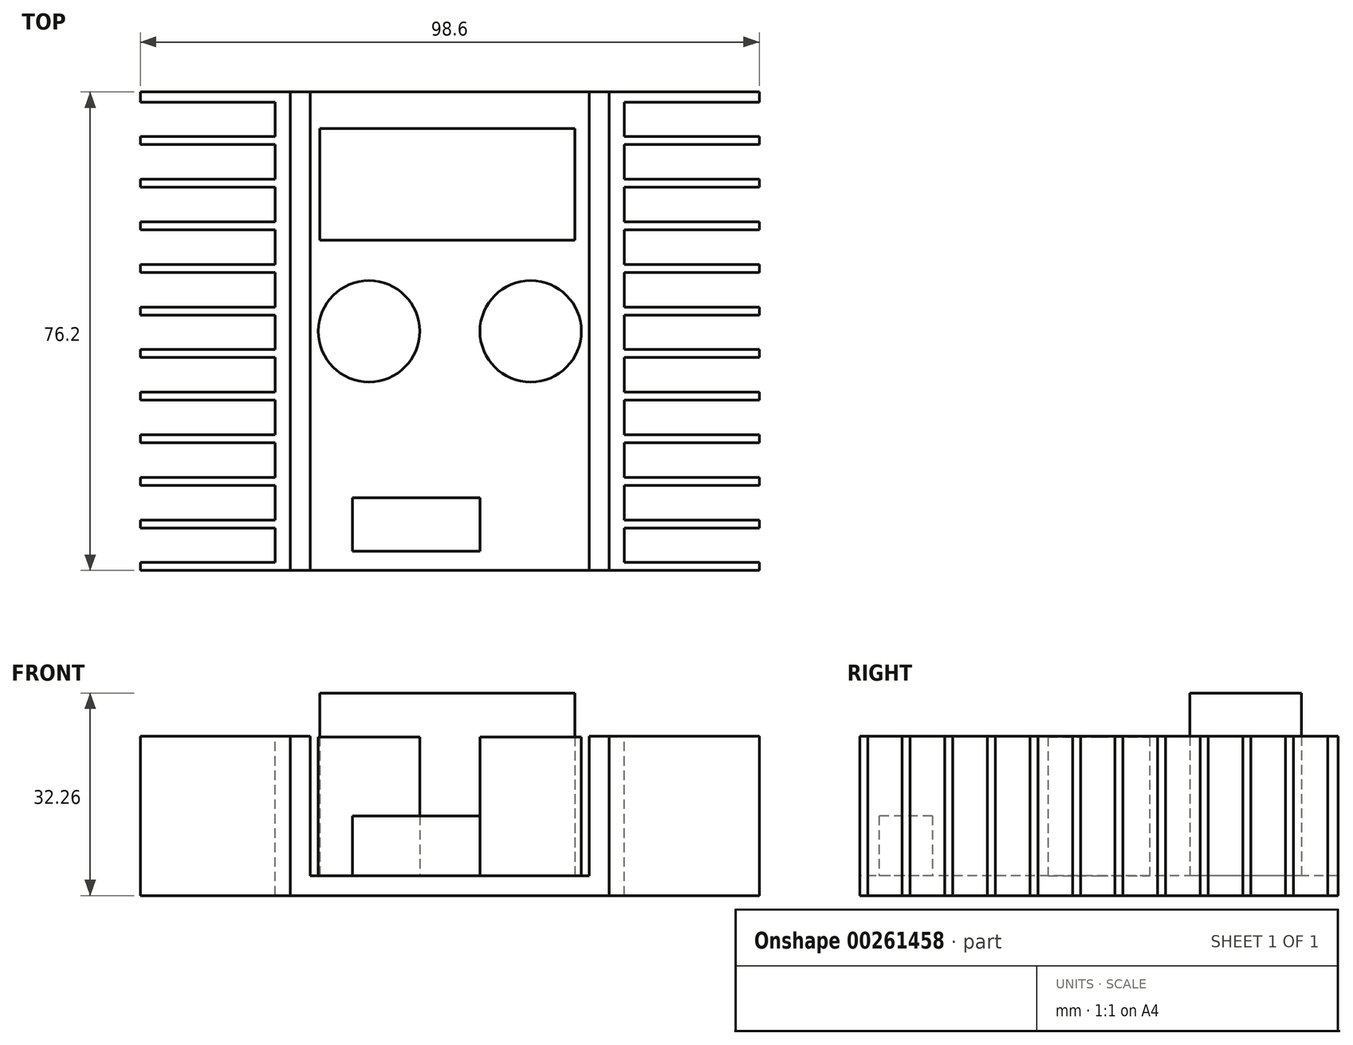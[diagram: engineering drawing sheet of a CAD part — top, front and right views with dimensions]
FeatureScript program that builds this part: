
annotation { "Feature Type Name" : "Feature", "Feature Type Description" : "" }
export const myFeature = defineFeature(function(context is Context, id is Id, definition is map)
    precondition{}
    {
        {
            var Q0;
            Q0=qCreatedBy(makeId("Top.planeOp"),FACE);
            var sketch = newSketch(context, id + "F0", { "sketchPlane" : qUnion([Q0])});
            skLineSegment(sketch, "E0.bottom", {"start": v(0, 0) * mm, "end": v(50.8, 0) * mm});
            skLineSegment(sketch, "E0.top", {"start": v(0, 76.2) * mm, "end": v(50.8, 76.2) * mm});
            skLineSegment(sketch, "E0.left", {"start": v(0, 0) * mm, "end": v(0, 76.2) * mm});
            skLineSegment(sketch, "E0.right", {"start": v(50.8, 0) * mm, "end": v(50.8, 76.2) * mm});
            skSolve(sketch);
        }
        {
            var Q0;
            Q0 = qSketchRegion(id + "F0", true);
            extrude(context, id + "F1", {"entities" : qUnion([Q0]), "depth" : 25.4 * mm});
        }
        {
            var Q0;
            Q0=makeQuery(id+"F1.opExtrude","SWEPT_FACE",FACE,{"disambiguationData":[OSD([sQuery(id+"F0.wireOp",EDGE,"E0.bottom")])]});
            var sketch = newSketch(context, id + "F2", { "sketchPlane" : qUnion([Q0])});
            skLineSegment(sketch, "E1.bottom", {"start": v(3.17, 40.7) * mm, "end": v(47.63, 40.7) * mm});
            skLineSegment(sketch, "E1.top", {"start": v(3.17, 3.17) * mm, "end": v(47.63, 3.18) * mm});
            skLineSegment(sketch, "E1.left", {"start": v(3.17, 40.7) * mm, "end": v(3.17, 3.17) * mm});
            skLineSegment(sketch, "E1.right", {"start": v(47.63, 40.7) * mm, "end": v(47.63, 3.18) * mm});
            skSolve(sketch);
        }
        {
            var Q0;
            Q0 = qSketchRegion(id + "F2", true);
            extrude(context, id + "F3", {"entities" : qUnion([Q0]), "operationType" : NewBodyOperationType.REMOVE, "endBound" : BoundingType.THROUGH_ALL, "oppositeDirection" : true, "depth" : 25.4 * mm});
        }
        {
            var Q0;
            {var subQ0=sQuery(id+"F0.wireOp",EDGE,"E0.bottom");var subQ1=sQuery(id+"F0.wireOp",EDGE,"E0.top");var subQ2=sQuery(id+"F0.wireOp",EDGE,"E0.right");Q0=makeQuery(id+"F3.boolean.opBoolean","SPLIT",FACE,{"disambiguationData":[TD([makeQuery(id+"F1.opExtrude","SWEPT_FACE",FACE,{"disambiguationData":[OSD([subQ2])]})])],"derivedFrom":makeQuery(id+"F1.opExtrude","CAP_FACE",FACE,{"disambiguationData":[OSD([subQ0,subQ1,sQuery(id+"F0.wireOp",EDGE,"E0.left"),subQ2])],"isStart":false})});}
            var sketch = newSketch(context, id + "F4", { "sketchPlane" : qUnion([Q0])});
            skLineSegment(sketch, "E2.bottom", {"start": v(50.8, 76.2) * mm, "end": v(74.7, 76.2) * mm});
            skLineSegment(sketch, "E2.top", {"start": v(50.8, 0) * mm, "end": v(74.7, 0) * mm});
            skLineSegment(sketch, "E2.left", {"start": v(50.8, 76.2) * mm, "end": v(50.8, 0) * mm});
            skLineSegment(sketch, "E2.right", {"start": v(74.7, 76.2) * mm, "end": v(74.7, 74.6) * mm});
            skLineSegment(sketch, "E3.bottom", {"start": v(74.7, 6.78) * mm, "end": v(53.21, 6.78) * mm});
            skLineSegment(sketch, "E3.top", {"start": v(74.7, 1.27) * mm, "end": v(53.21, 1.27) * mm});
            skLineSegment(sketch, "E3.right", {"start": v(53.21, 6.78) * mm, "end": v(53.21, 1.27) * mm});
            skLineSegment(sketch, "E4.0.1.0", {"start": v(74.7, 13.56) * mm, "end": v(53.21, 13.56) * mm});
            skLineSegment(sketch, "E4.0.1.1", {"start": v(53.21, 13.56) * mm, "end": v(53.21, 8.05) * mm});
            skLineSegment(sketch, "E4.0.1.2", {"start": v(74.7, 8.05) * mm, "end": v(53.21, 8.05) * mm});
            skLineSegment(sketch, "E4.0.2.0", {"start": v(74.7, 20.35) * mm, "end": v(53.21, 20.35) * mm});
            skLineSegment(sketch, "E4.0.2.1", {"start": v(53.21, 20.35) * mm, "end": v(53.21, 14.83) * mm});
            skLineSegment(sketch, "E4.0.2.2", {"start": v(74.7, 14.83) * mm, "end": v(53.21, 14.83) * mm});
            skLineSegment(sketch, "E4.0.3.0", {"start": v(74.7, 27.13) * mm, "end": v(53.21, 27.13) * mm});
            skLineSegment(sketch, "E4.0.3.1", {"start": v(53.21, 27.13) * mm, "end": v(53.21, 21.62) * mm});
            skLineSegment(sketch, "E4.0.3.2", {"start": v(74.7, 21.62) * mm, "end": v(53.21, 21.62) * mm});
            skLineSegment(sketch, "E4.0.4.0", {"start": v(74.7, 33.9) * mm, "end": v(53.21, 33.9) * mm});
            skLineSegment(sketch, "E4.0.4.1", {"start": v(53.21, 33.9) * mm, "end": v(53.21, 28.4) * mm});
            skLineSegment(sketch, "E4.0.4.2", {"start": v(74.7, 28.4) * mm, "end": v(53.21, 28.4) * mm});
            skLineSegment(sketch, "E4.0.5.0", {"start": v(74.7, 40.7) * mm, "end": v(53.21, 40.7) * mm});
            skLineSegment(sketch, "E4.0.5.1", {"start": v(53.21, 40.7) * mm, "end": v(53.21, 35.18) * mm});
            skLineSegment(sketch, "E4.0.5.2", {"start": v(74.7, 35.18) * mm, "end": v(53.21, 35.18) * mm});
            skLineSegment(sketch, "E4.0.6.0", {"start": v(74.7, 47.47) * mm, "end": v(53.21, 47.47) * mm});
            skLineSegment(sketch, "E4.0.6.1", {"start": v(53.21, 47.47) * mm, "end": v(53.21, 41.96) * mm});
            skLineSegment(sketch, "E4.0.6.2", {"start": v(74.7, 41.96) * mm, "end": v(53.21, 41.96) * mm});
            skLineSegment(sketch, "E4.0.7.0", {"start": v(74.7, 54.25) * mm, "end": v(53.21, 54.25) * mm});
            skLineSegment(sketch, "E4.0.7.1", {"start": v(53.21, 54.25) * mm, "end": v(53.21, 48.74) * mm});
            skLineSegment(sketch, "E4.0.7.2", {"start": v(74.7, 48.74) * mm, "end": v(53.21, 48.74) * mm});
            skLineSegment(sketch, "E4.0.8.0", {"start": v(74.7, 61.04) * mm, "end": v(53.21, 61.04) * mm});
            skLineSegment(sketch, "E4.0.8.1", {"start": v(53.21, 61.04) * mm, "end": v(53.21, 55.52) * mm});
            skLineSegment(sketch, "E4.0.8.2", {"start": v(74.7, 55.52) * mm, "end": v(53.21, 55.52) * mm});
            skLineSegment(sketch, "E4.0.9.0", {"start": v(74.7, 67.82) * mm, "end": v(53.21, 67.82) * mm});
            skLineSegment(sketch, "E4.0.9.1", {"start": v(53.21, 67.82) * mm, "end": v(53.21, 62.3) * mm});
            skLineSegment(sketch, "E4.0.9.2", {"start": v(74.7, 62.3) * mm, "end": v(53.21, 62.3) * mm});
            skLineSegment(sketch, "E4.0.10.0", {"start": v(74.7, 74.6) * mm, "end": v(53.21, 74.6) * mm});
            skLineSegment(sketch, "E4.0.10.1", {"start": v(53.21, 74.6) * mm, "end": v(53.21, 69.09) * mm});
            skLineSegment(sketch, "E4.0.10.2", {"start": v(74.7, 69.09) * mm, "end": v(53.21, 69.09) * mm});
            skLineSegment(sketch, "E4.direction1", {"start": v(53.21, 1.27) * mm, "end": v(74.7, 1.27) * mm, "construction": true});
            skLineSegment(sketch, "E4.direction2", {"start": v(53.21, 1.27) * mm, "end": v(53.21, 8.05) * mm, "construction": true});
            skPoint(sketch, "E5.orphan", {"position": v(78.79, 6.78) * mm});
            skLineSegment(sketch, "E6.trimOffspring", {"start": v(74.7, 1.27) * mm, "end": v(74.7, 0) * mm});
            skPoint(sketch, "E7.orphan", {"position": v(78.79, 1.27) * mm});
            skLineSegment(sketch, "E8.trimOffspring", {"start": v(74.7, 8.05) * mm, "end": v(74.7, 6.78) * mm});
            skLineSegment(sketch, "E9.trimOffspring", {"start": v(74.7, 14.83) * mm, "end": v(74.7, 13.56) * mm});
            skLineSegment(sketch, "E10.trimOffspring", {"start": v(74.7, 21.62) * mm, "end": v(74.7, 20.35) * mm});
            skLineSegment(sketch, "E11.trimOffspring", {"start": v(74.7, 28.4) * mm, "end": v(74.7, 27.13) * mm});
            skLineSegment(sketch, "E12.trimOffspring", {"start": v(74.7, 35.18) * mm, "end": v(74.7, 33.9) * mm});
            skLineSegment(sketch, "E13.trimOffspring", {"start": v(74.7, 41.96) * mm, "end": v(74.7, 40.7) * mm});
            skLineSegment(sketch, "E14.trimOffspring", {"start": v(74.7, 48.74) * mm, "end": v(74.7, 47.47) * mm});
            skLineSegment(sketch, "E15.trimOffspring", {"start": v(74.7, 55.52) * mm, "end": v(74.7, 54.25) * mm});
            skPoint(sketch, "E16.orphan", {"position": v(78.79, 8.05) * mm});
            skPoint(sketch, "E17.orphan", {"position": v(78.79, 13.56) * mm});
            skPoint(sketch, "E18.orphan", {"position": v(78.79, 14.83) * mm});
            skPoint(sketch, "E19.orphan", {"position": v(78.79, 20.35) * mm});
            skPoint(sketch, "E20.orphan", {"position": v(78.79, 21.62) * mm});
            skPoint(sketch, "E21.orphan", {"position": v(78.79, 28.4) * mm});
            skPoint(sketch, "E22.orphan", {"position": v(78.79, 27.13) * mm});
            skPoint(sketch, "E23.orphan", {"position": v(78.79, 33.9) * mm});
            skPoint(sketch, "E24.orphan", {"position": v(78.79, 35.18) * mm});
            skPoint(sketch, "E25.orphan", {"position": v(78.79, 40.7) * mm});
            skPoint(sketch, "E26.orphan", {"position": v(78.79, 41.96) * mm});
            skPoint(sketch, "E27.orphan", {"position": v(78.79, 48.74) * mm});
            skPoint(sketch, "E28.orphan", {"position": v(78.79, 47.47) * mm});
            skPoint(sketch, "E29.orphan", {"position": v(78.79, 54.25) * mm});
            skLineSegment(sketch, "E30.trimOffspring", {"start": v(74.7, 69.09) * mm, "end": v(74.7, 67.82) * mm});
            skLineSegment(sketch, "E31.trimOffspring", {"start": v(74.7, 62.3) * mm, "end": v(74.7, 61.04) * mm});
            skPoint(sketch, "E32.orphan", {"position": v(78.79, 61.04) * mm});
            skPoint(sketch, "E33.orphan", {"position": v(78.79, 74.6) * mm});
            skPoint(sketch, "E34.orphan", {"position": v(78.79, 69.09) * mm});
            skPoint(sketch, "E35.orphan", {"position": v(78.79, 67.82) * mm});
            skPoint(sketch, "E36.orphan", {"position": v(78.79, 62.3) * mm});
            skSolve(sketch);
        }
        {
            var Q0;
            Q0 = qSketchRegion(id + "F4", true);
            var Q1;
            Q1=makeQuery(id+"F1.opExtrude","CAP_FACE",FACE,{"disambiguationData":[OSD([sQuery(id+"F0.wireOp",EDGE,"E0.bottom"),sQuery(id+"F0.wireOp",EDGE,"E0.top"),sQuery(id+"F0.wireOp",EDGE,"E0.left"),sQuery(id+"F0.wireOp",EDGE,"E0.right")])],"isStart":true});
            extrude(context, id + "F5", {"entities" : qUnion([Q0]), "endBound" : BoundingType.UP_TO_SURFACE, "oppositeDirection" : true, "endBoundEntityFace" : qUnion([Q1]), "depth" : 25.4 * mm});
        }
        {
            var Q0;
            Q0=qCreatedBy(makeId("Right.planeOp"),FACE);
            cPlane(context, id + "F6", {"entities" : qUnion([Q0]), "cplaneType" : CPlaneType.OFFSET, "offset" : 25.4 * mm, "width" : 152.4 * mm, "height" : 152.4 * mm});
        }
        {
            var Q0;
            Q0=makeQuery(id+"F5.opExtrude","SWEPT_BODY",BODY,{"disambiguationData":[OSD([sQuery(id+"F4.wireOp",EDGE,"E2.bottom"),sQuery(id+"F4.wireOp",EDGE,"E2.top"),sQuery(id+"F4.wireOp",EDGE,"E2.left"),sQuery(id+"F4.wireOp",EDGE,"E2.right"),sQuery(id+"F4.wireOp",EDGE,"E3.bottom"),sQuery(id+"F4.wireOp",EDGE,"E3.top"),sQuery(id+"F4.wireOp",EDGE,"E3.right"),sQuery(id+"F4.wireOp",EDGE,"E4.0.1.0"),sQuery(id+"F4.wireOp",EDGE,"E4.0.1.1"),sQuery(id+"F4.wireOp",EDGE,"E4.0.1.2"),sQuery(id+"F4.wireOp",EDGE,"E4.0.2.0"),sQuery(id+"F4.wireOp",EDGE,"E4.0.2.1"),sQuery(id+"F4.wireOp",EDGE,"E4.0.2.2"),sQuery(id+"F4.wireOp",EDGE,"E4.0.3.0"),sQuery(id+"F4.wireOp",EDGE,"E4.0.3.1"),sQuery(id+"F4.wireOp",EDGE,"E4.0.3.2"),sQuery(id+"F4.wireOp",EDGE,"E4.0.4.0"),sQuery(id+"F4.wireOp",EDGE,"E4.0.4.1"),sQuery(id+"F4.wireOp",EDGE,"E4.0.4.2"),sQuery(id+"F4.wireOp",EDGE,"E4.0.5.0"),sQuery(id+"F4.wireOp",EDGE,"E4.0.5.1"),sQuery(id+"F4.wireOp",EDGE,"E4.0.5.2"),sQuery(id+"F4.wireOp",EDGE,"E4.0.6.0"),sQuery(id+"F4.wireOp",EDGE,"E4.0.6.1"),sQuery(id+"F4.wireOp",EDGE,"E4.0.6.2"),sQuery(id+"F4.wireOp",EDGE,"E4.0.7.0"),sQuery(id+"F4.wireOp",EDGE,"E4.0.7.1"),sQuery(id+"F4.wireOp",EDGE,"E4.0.7.2"),sQuery(id+"F4.wireOp",EDGE,"E4.0.8.0"),sQuery(id+"F4.wireOp",EDGE,"E4.0.8.1"),sQuery(id+"F4.wireOp",EDGE,"E4.0.8.2"),sQuery(id+"F4.wireOp",EDGE,"E4.0.9.0"),sQuery(id+"F4.wireOp",EDGE,"E4.0.9.1"),sQuery(id+"F4.wireOp",EDGE,"E4.0.9.2"),sQuery(id+"F4.wireOp",EDGE,"E4.0.10.0"),sQuery(id+"F4.wireOp",EDGE,"E4.0.10.1"),sQuery(id+"F4.wireOp",EDGE,"E4.0.10.2"),sQuery(id+"F4.wireOp",EDGE,"E6.trimOffspring"),sQuery(id+"F4.wireOp",EDGE,"E8.trimOffspring"),sQuery(id+"F4.wireOp",EDGE,"E9.trimOffspring"),sQuery(id+"F4.wireOp",EDGE,"E10.trimOffspring"),sQuery(id+"F4.wireOp",EDGE,"E11.trimOffspring"),sQuery(id+"F4.wireOp",EDGE,"E12.trimOffspring"),sQuery(id+"F4.wireOp",EDGE,"E13.trimOffspring"),sQuery(id+"F4.wireOp",EDGE,"E14.trimOffspring"),sQuery(id+"F4.wireOp",EDGE,"E15.trimOffspring"),sQuery(id+"F4.wireOp",EDGE,"E30.trimOffspring"),sQuery(id+"F4.wireOp",EDGE,"E31.trimOffspring")])]});
            var Q1;
            Q1=qCreatedBy(id+"F6.planeOp",FACE);
            mirror(context, id + "F7", {"entities" : qUnion([Q0]), "mirrorPlane" : qUnion([Q1])});
        }
        {
            var Q0;
            Q0=makeQuery(id+"F3.boolean.opBoolean","COPY",FACE,{"derivedFrom":makeQuery(id+"F3.opExtrude","SWEPT_FACE",FACE,{"disambiguationData":[OSD([sQuery(id+"F2.wireOp",EDGE,"E1.top")])]})});
            var sketch = newSketch(context, id + "F8", { "sketchPlane" : qUnion([Q0])});
            skCircle(sketch, "E37", {"center": v(12.52, 38.1) * mm, "radius": 8.08 * mm});
            skCircle(sketch, "E38", {"center": v(38.28, 38.1) * mm, "radius": 8.08 * mm});
            skSolve(sketch);
        }
        {
            var Q0;
            Q0 = qSketchRegion(id + "F8", true);
            extrude(context, id + "F9", {"entities" : qUnion([Q0]), "depth" : 22.1 * mm});
        }
        {
            var Q0;
            Q0=makeQuery(id+"F3.boolean.opBoolean","COPY",FACE,{"derivedFrom":makeQuery(id+"F3.opExtrude","SWEPT_FACE",FACE,{"disambiguationData":[OSD([sQuery(id+"F2.wireOp",EDGE,"E1.top")])]})});
            var sketch = newSketch(context, id + "F10", { "sketchPlane" : qUnion([Q0])});
            skLineSegment(sketch, "E39.bottom", {"start": v(9.9, 11.56) * mm, "end": v(30.23, 11.56) * mm});
            skLineSegment(sketch, "E39.top", {"start": v(9.9, 3.05) * mm, "end": v(30.23, 3.05) * mm});
            skLineSegment(sketch, "E39.left", {"start": v(9.9, 11.56) * mm, "end": v(9.9, 3.05) * mm});
            skLineSegment(sketch, "E39.right", {"start": v(30.23, 11.56) * mm, "end": v(30.23, 3.05) * mm});
            skSolve(sketch);
        }
        {
            var Q0;
            Q0 = qSketchRegion(id + "F10", true);
            extrude(context, id + "F11", {"entities" : qUnion([Q0]), "depth" : 9.52 * mm});
        }
        {
            var Q0;
            Q0=makeQuery(id+"F3.boolean.opBoolean","COPY",FACE,{"derivedFrom":makeQuery(id+"F3.opExtrude","SWEPT_FACE",FACE,{"disambiguationData":[OSD([sQuery(id+"F2.wireOp",EDGE,"E1.top")])]})});
            var sketch = newSketch(context, id + "F12", { "sketchPlane" : qUnion([Q0])});
            skLineSegment(sketch, "E40.bottom", {"start": v(4.7, 70.36) * mm, "end": v(45.34, 70.36) * mm});
            skLineSegment(sketch, "E40.top", {"start": v(4.7, 52.58) * mm, "end": v(45.34, 52.58) * mm});
            skLineSegment(sketch, "E40.left", {"start": v(4.7, 70.36) * mm, "end": v(4.7, 52.58) * mm});
            skLineSegment(sketch, "E40.right", {"start": v(45.34, 70.36) * mm, "end": v(45.34, 52.58) * mm});
            skSolve(sketch);
        }
        {
            var Q0;
            Q0 = qSketchRegion(id + "F12", true);
            extrude(context, id + "F13", {"entities" : qUnion([Q0]), "depth" : 29.08 * mm});
        }
    });
